# Revit family: ISI_IdealStandard_CounterTopWashbasins_Dea_T0443
name_source: partatom
category: Plumbing Fixtures
revit_build: Autodesk Revit MEP 2012 (Build: 20110309_2315(x64)
units: mm (PartAtom-declared; Revit-internal decimal feet)

## types (2) — shared parameters
Accessories = www.idealspec.co.uk
AreaUnits = millimeters
Assembly Code = C1030200
AssetType = Fixed
Brand = Ideal Standard
Category = SanitaryTerminal_WASHHANDBASIN_UK
Color = White
ConnectionType = Plumbing
Default Elevation = 800 mm  [stored 2.62467 ft]
DrainSize = 32 mm  [stored 0.104987 ft]
DurationUnit = year
ECA = No
ExpectedLife = 30
Features = Vessel washbasin
Finish = White
IfcExportAs = IfcSanitaryTerminalType
IfcExportType = WASHHANDBASIN
InstallationInstructions = www.idealspec.co.uk/resources.html
LinearUnits = millimeters
ManufacturerURL = www.idealspec.co.uk
Material = Vitreous china
NBSDescription = Counter top washbasins
NBSReference = 45-35-70/360
NettWeight = 9 Kg
NominalDepth = 333 mm
NominalHeight = 122 mm
NominalLength = 333 mm
NominalWidth = 525 mm
Shape = Sculptured
Size = 122 x 333 x 525 mm
Space = Internal
SpareParts = www.fastpart-spares.co.uk
URL = www.idealspec.co.uk
Uniclass2 = Pr_40_20_96_18
Version = 2
VolumeUnits = Litres
WRAS = No
WarrantyDescription = Manufacturers Warranty
WarrantyDurationParts = 99
WarrantyDurationUnit = year
WashHandBasinMounting = CounterTop
WashHandBasinType = HandRinse
WasteCover = ISI_IdealStandard_BasinMaterial_White3_Render
WaterEfficientProduct = No
zero-valued in all types: CWFU, Cost, HWFU, WFU

## per-type parameters (varying)
| type | BIMObjectName | Description | Model | ModelNumber | ModelReference | Name | ProductInformation |
| T044301 - Dea 52cm Vessel Washbasin - Gloss | ISI_IdealStandard_CounterTopWashbasins_Dea_T044301 | Dea 52 cm vessel washbasin - gloss finish | T044301 | T044301 | Dea 52 cm vessel washbasin - gloss finish | CounterTopWashBasins_Washbasins_Dea_T044301_IdealStandard | www.idealspec.co.uk/assets/datasheet/T044301 |
| T044383 - Dea 52cm Vessel Washbasin - Matte | ISI_IdealStandard_CounterTopWashbasins_Dea_T044383 | Dea 52 cm vessel washbasin - matte finish | T044383 | T044383 | Dea 52 cm vessel washbasin - matte finish | CounterTopWashBasins_Washbasins_Dea_T044383_IdealStandard | www.idealspec.co.uk/assets/datasheet/T044383 |

note: [stored X ft] marks values corroborated as IEEE doubles in the binary element streams (Revit-internal decimal feet)

## geometry (parser evidence)
native form markers: Sweep x2
no freeform markers — native parametric forms only
